# Revit family: ok-Celite_City_Bacia com Caixa Acoplada_20351
name_source: partatom
category: Plumbing Fixtures
revit_build: Autodesk Revit MEP 2014 (Build: 20131024_2115(x64)
units: mm (PartAtom-declared; Revit-internal decimal feet)

## types (5) — shared parameters
Assembly Code = D2010100
CWFU = 1
Celite: Categoria = Linhas Completas
Celite: Código = 20351
Celite: Desenho Técnico = http://www.celite.com.br
Celite: Fabricante = Celite
Celite: Linha = City
Celite: Link do Produto = http://www.celite.com.br
Celite: Norma = ABNT NBR 15097-1:2011/ABNT NBR 15097-2:2011 - fabricação/instalação
Celite: Produto = Louças
Celite: Tipo = Bacias com caixas
Celite: Versão = Autodesk Revit MEP 2014
Desenvolvido por = ofcdesk
Diâmetro Ponto de Esgoto = 100 mm
Manufacturer = Celite
Model = 20351
Raio Ponto de Esgoto = 50 mm
Raio Ponto de Água = 10 mm
Selo de Qualidade ofcdesk = Standard
URL = http://www.celite.com.br
WFU = 3
zero-valued in all types: Default Elevation

## per-type parameters (varying)
| type | Celite: Cores Disponíveis | Celite: Descrição | Description | Tipo de assento | Tipo de caixa |
| Branca - 20351 com Caixa Ecoflush e Assento PP | Branco | Bacia com caixa acoplada Ecoflush - 3 e 6 litros cor branca (20351), Caixa Ecoflush e Assento PP, linha City - Louças Celite | Bacia com caixa acoplada Ecoflush - 3 e 6 litros cor branca (20351), Caixa Ecoflush e Assento PP, linha City - Louças Celite | Celite_City_Assento para Bacia Sanitária_20981 : Branco - 20981 | Celite_City_Caixa para Acoplar_20570 : Branco - 20570 |
| Preta - 20351 com Caixa Ecoflush e Assento PP | Preto | Bacia com caixa acoplada Ecoflush - 3 e 6 litros cor preta (20351), Caixa Ecoflush e Assento PP, linha City - Louças Celite | Bacia com caixa acoplada Ecoflush - 3 e 6 litros cor preta (20351), Caixa Ecoflush e Assento PP, linha City - Louças Celite | Celite_City_Assento para Bacia Sanitária_20981 : Preto - 20981 | Celite_City_Caixa para Acoplar_20570 : Preto - 20570 |
| Pergamon - 20351 com Caixa Ecoflush e Assento PP | Pergamon | Bacia com caixa acoplada Ecoflush - 3 e 6 litros cor pergamon (20351), Caixa Ecoflush e Assento PP, linha City - Louças Celite | Bacia com caixa acoplada Ecoflush - 3 e 6 litros cor pergamon (20351), Caixa Ecoflush e Assento PP, linha City - Louças Celite | Celite_City_Assento para Bacia Sanitária_20981 : Pergamon - 20981 | Celite_City_Caixa para Acoplar_20570 : Pergamon - 20570 |
| Cinza prata - 20351 com Caixa Ecoflush e Assento PP | Cinza prata | Bacia com caixa acoplada Ecoflush - 3 e 6 litros cor cinza prata (20351), Caixa Ecoflush e Assento PP, linha City - Louças Celite | Bacia com caixa acoplada Ecoflush - 3 e 6 litros cor cinza prata (20351), Caixa Ecoflush e Assento PP, linha City - Louças Celite | Celite_City_Assento para Bacia Sanitária_20981 : Cinza prata - 20981 | Celite_City_Caixa para Acoplar_20570 : Cinza prata - 20570 |
| Branca - 20351 com Caixa Ecoflush e Assento PP Plus Softclose | Branco | Bacia com caixa acoplada Ecoflush - 3 e 6 litros cor branca (20351), Caixa Ecoflush e Assento PP Plus Softclose, linha City - Louças Celite | Bacia com caixa acoplada Ecoflush - 3 e 6 litros cor branca (20351), Caixa Ecoflush e Assento PP Plus Softclose, linha City - Louças Celite | Celite_Universal_Assento para Bacia Sanitária Soft Close_00988 : Branco - 00988 | Celite_City_Caixa para Acoplar_20570 : Branco - 20570 |

## geometry (parser evidence)
native form markers: Sweep x8
no freeform markers — native parametric forms only
